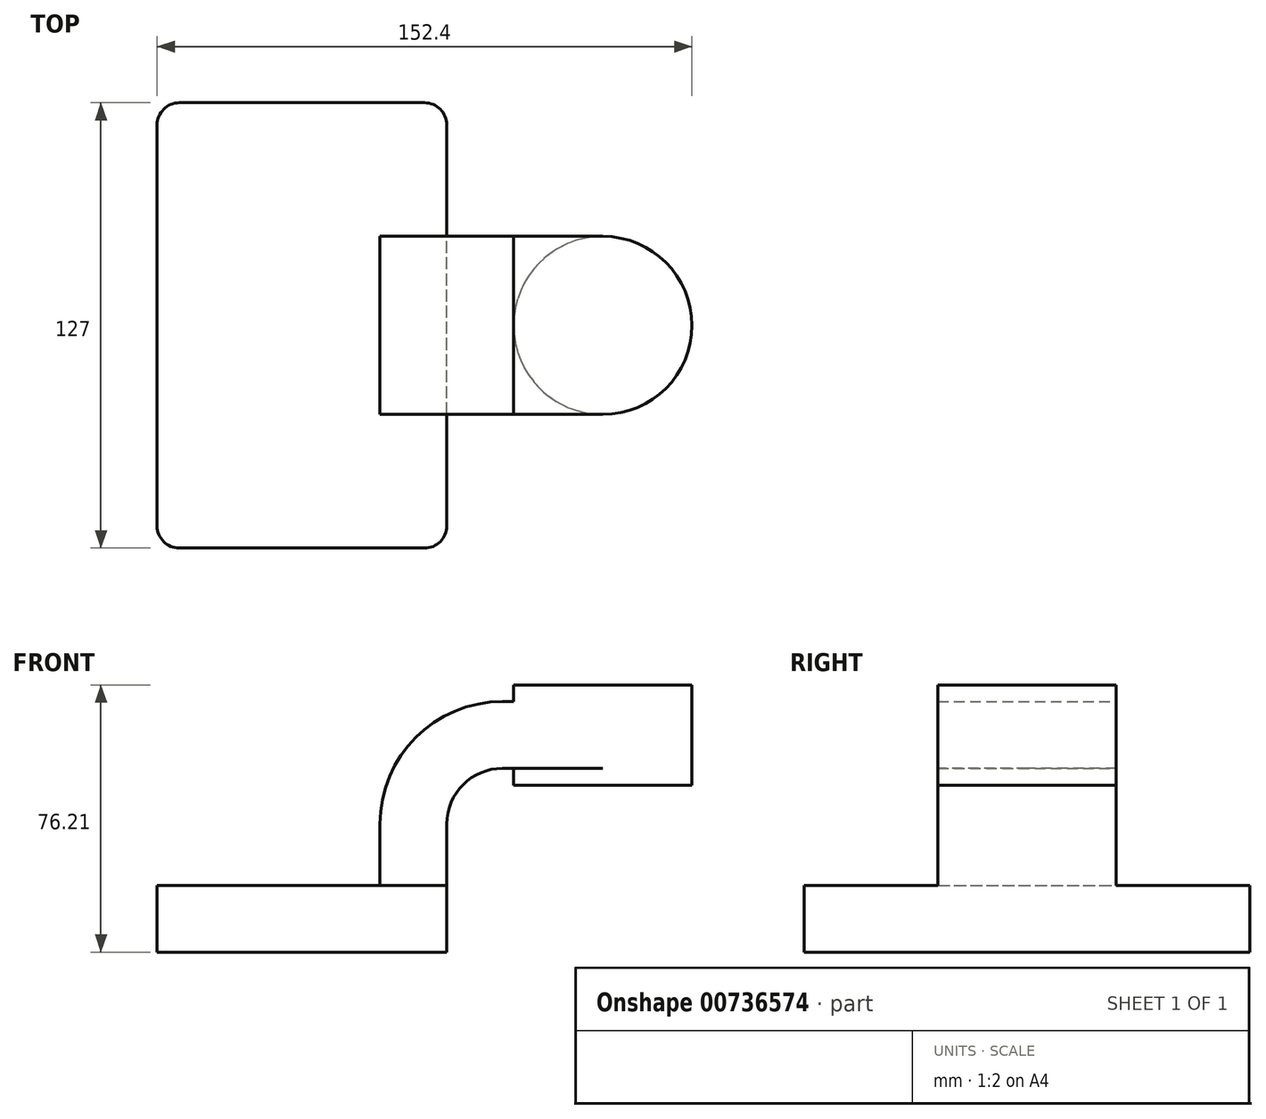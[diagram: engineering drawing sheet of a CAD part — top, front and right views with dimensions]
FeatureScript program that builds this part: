
annotation { "Feature Type Name" : "Feature", "Feature Type Description" : "" }
export const myFeature = defineFeature(function(context is Context, id is Id, definition is map)
    precondition{}
    {
        {
            var Q0;
            Q0=qCreatedBy(makeId("Front.planeOp"),FACE);
            var sketch = newSketch(context, id + "F0", { "sketchPlane" : qUnion([Q0])});
            skLineSegment(sketch, "E0.bottom", {"start": v(41.28, -9.52) * mm, "end": v(-41.28, -9.53) * mm});
            skLineSegment(sketch, "E0.top", {"start": v(41.28, 9.53) * mm, "end": v(-41.28, 9.53) * mm});
            skLineSegment(sketch, "E0.left", {"start": v(41.28, -9.52) * mm, "end": v(41.28, 9.53) * mm});
            skLineSegment(sketch, "E0.right", {"start": v(-41.28, -9.53) * mm, "end": v(-41.28, 9.53) * mm});
            skPoint(sketch, "E0.middle", {"position": v(0, 0) * mm});
            skLineSegment(sketch, "E1.bottom", {"start": v(111.12, 38.1) * mm, "end": v(60.33, 38.1) * mm});
            skLineSegment(sketch, "E1.top", {"start": v(111.12, 66.68) * mm, "end": v(60.33, 66.68) * mm});
            skLineSegment(sketch, "E1.left", {"start": v(111.12, 38.1) * mm, "end": v(111.12, 66.68) * mm});
            skLineSegment(sketch, "E1.right", {"start": v(60.33, 38.1) * mm, "end": v(60.33, 66.67) * mm});
            skPoint(sketch, "E1.middle", {"position": v(85.72, 52.39) * mm});
            skLineSegment(sketch, "E2", {"start": v(41.28, 9.53) * mm, "end": v(41.28, 27) * mm});
            skArc(sketch, "E3", {"start": v(41.27, 27) * mm, "mid": v(45.92, 38.23) * mm, "end": v(57.15, 42.88) * mm});
            skLineSegment(sketch, "E4", {"start": v(57.15, 42.88) * mm, "end": v(85.72, 42.88) * mm});
            skLineSegment(sketch, "E5.0", {"start": v(57.15, 61.93) * mm, "end": v(85.34, 61.93) * mm});
            skArc(sketch, "E5.1", {"start": v(22.23, 27) * mm, "mid": v(32.45, 51.7) * mm, "end": v(57.15, 61.93) * mm});
            skLineSegment(sketch, "E5.2", {"start": v(22.22, 9.53) * mm, "end": v(22.22, 27) * mm});
            skLineSegment(sketch, "E6", {"start": v(85.72, 38.1) * mm, "end": v(85.72, 66.68) * mm});
            skFitSpline(sketch, "E7", {"points": [v(-41.28, 9.52) * mm, v(57.15, 61.93) * mm], "startDerivative": vector(1.8, 79.24) * mm, "endDerivative": vector(102.68, -1.9) * mm});
            skSolve(sketch);
        }
        {
            var Q0;
            Q0=makeQuery(id+"F0.imprint","IMPRINT",FACE,{"disambiguationData":[TD([[makeQuery(id+"F0.imprint","IMPRINT",EDGE,{"derivedFrom":sQuery(id+"F0.wireOp",EDGE,"E0.bottom")}),-1.0]])]});
            extrude(context, id + "F1", {"entities" : qUnion([Q0]), "endBound" : BoundingType.SYMMETRIC, "depth" : 127 * mm, "offsetDistance" : 25.4 * mm});
        }
        {
            var Q0;
            {var subQ1=sQuery(id+"F0.wireOp",EDGE,"E2");Q0=makeQuery(id+"F0.imprint","IMPRINT",FACE,{"disambiguationData":[TD([[makeQuery(id+"F0.imprint","IMPRINT",EDGE,{"derivedFrom":subQ1}),1.0]])]});}
            var Q1;
            {var subQ0=sQuery(id+"F0.wireOp",EDGE,"E1.right");var subQ1=sQuery(id+"F0.wireOp",EDGE,"E1.top");var subQ2=makeQuery(id+"F0.imprint","INTERSECT",VERTEX,{"derivedFrom":[subQ1,subQ0]});Q1=makeQuery(id+"F0.imprint","IMPRINT",FACE,{"disambiguationData":[TD([[makeQuery(id+"F0.imprint","IMPRINT",EDGE,{"disambiguationData":[TD([[subQ2,1.0]])],"derivedFrom":subQ1}),1.0]])]});}
            extrude(context, id + "F2", {"entities" : qUnion([Q0, Q1]), "operationType" : NewBodyOperationType.ADD, "endBound" : BoundingType.SYMMETRIC, "depth" : 50.8 * mm, "offsetDistance" : 25.4 * mm});
        }
        {
            var Q0;
            Q0=makeQuery(id+"F0.imprint","IMPRINT",FACE,{"disambiguationData":[TD([[makeQuery(id+"F0.imprint","IMPRINT",EDGE,{"derivedFrom":sQuery(id+"F0.wireOp",EDGE,"E5.1")}),1.0]])]});
            extrude(context, id + "F3", {"entities" : qUnion([Q0]), "operationType" : NewBodyOperationType.ADD, "endBound" : BoundingType.SYMMETRIC, "depth" : 15.88 * mm, "offsetDistance" : 25.4 * mm});
        }
        {
            var Q0;
            {var subQ0=sQuery(id+"F0.wireOp",EDGE,"E1.left");Q0=makeQuery(id+"F0.imprint","IMPRINT",FACE,{"disambiguationData":[TD([[makeQuery(id+"F0.imprint","IMPRINT",EDGE,{"derivedFrom":subQ0}),1.0]])]});}
            var Q1;
            Q1=sQuery(id+"F0.wireOp",EDGE,"E6");
            revolve(context, id + "F4", {"operationType" : NewBodyOperationType.ADD, "surfaceOperationType" : NewSurfaceOperationType.NEW, "entities" : qUnion([Q0]), "axis" : qUnion([Q1]), "revolveType" : RevolveType.FULL});
        }
        {
            var Q0;
            Q0=makeQuery(id+"F1.opExtrude","CAP_EDGE",EDGE,{"disambiguationData":[OSD([sQuery(id+"F0.wireOp",EDGE,"E0.right")])],"isStart":false});
            var Q1;
            Q1=makeQuery(id+"F1.opExtrude","CAP_EDGE",EDGE,{"disambiguationData":[OSD([sQuery(id+"F0.wireOp",EDGE,"E0.left")])],"isStart":false});
            var Q2;
            Q2=makeQuery(id+"F1.opExtrude","CAP_EDGE",EDGE,{"disambiguationData":[OSD([sQuery(id+"F0.wireOp",EDGE,"E0.left")])],"isStart":true});
            var Q3;
            Q3=makeQuery(id+"F1.opExtrude","CAP_EDGE",EDGE,{"disambiguationData":[OSD([sQuery(id+"F0.wireOp",EDGE,"E0.right")])],"isStart":true});
            fillet(context, id + "F5", {"entities" : qUnion([Q0, Q1, Q2, Q3]), "radius" : 6.35 * mm, "tangentPropagation" : true, "allowEdgeOverflow" : false});
        }
    });
